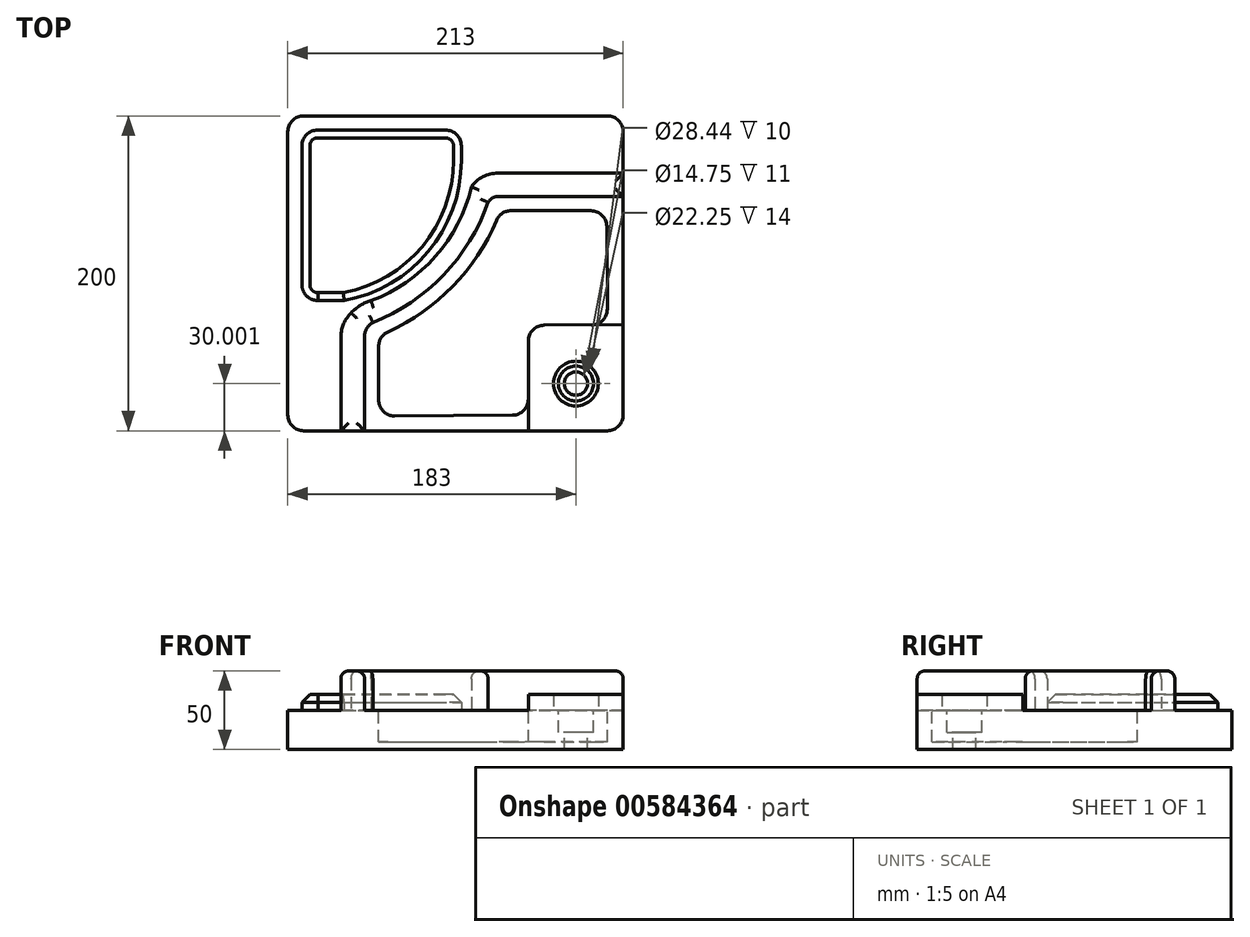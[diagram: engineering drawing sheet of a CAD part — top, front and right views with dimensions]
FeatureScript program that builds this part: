
annotation { "Feature Type Name" : "Feature", "Feature Type Description" : "" }
export const myFeature = defineFeature(function(context is Context, id is Id, definition is map)
    precondition{}
    {
        {
            var Q0;
            Q0=qCreatedBy(makeId("Top.planeOp"),FACE);
            var sketch = newSketch(context, id + "F0", { "sketchPlane" : qUnion([Q0])});
            skLineSegment(sketch, "E0.bottom", {"start": v(10, -74.9) * mm, "end": v(203, -74.9) * mm});
            skLineSegment(sketch, "E0.top", {"start": v(10, 125.1) * mm, "end": v(203, 125.1) * mm});
            skLineSegment(sketch, "E0.left", {"start": v(0, -64.9) * mm, "end": v(0, 115.1) * mm});
            skLineSegment(sketch, "E0.right", {"start": v(213, -64.9) * mm, "end": v(213, 115.1) * mm});
            skPoint(sketch, "E1.visualSharp", {"position": v(0, 125.1) * mm});
            skArc(sketch, "E1.filletArc", {"start": v(10, 125.1) * mm, "mid": v(2.93, 122.16) * mm, "end": v(0, 115.1) * mm});
            skPoint(sketch, "E2.visualSharp", {"position": v(213, 125.1) * mm});
            skArc(sketch, "E2.filletArc", {"start": v(213, 115.1) * mm, "mid": v(210.07, 122.16) * mm, "end": v(203, 125.1) * mm});
            skPoint(sketch, "E3.visualSharp", {"position": v(213, -74.9) * mm});
            skArc(sketch, "E3.filletArc", {"start": v(203, -74.9) * mm, "mid": v(210.07, -71.98) * mm, "end": v(213, -64.9) * mm});
            skPoint(sketch, "E4.visualSharp", {"position": v(0, -74.9) * mm});
            skArc(sketch, "E4.filletArc", {"start": v(0, -64.9) * mm, "mid": v(2.93, -71.98) * mm, "end": v(10, -74.9) * mm});
            skPoint(sketch, "E5.visualSharp", {"position": v(9, 116.1) * mm});
            skLineSegment(sketch, "E6", {"start": v(9, 17.87) * mm, "end": v(9, 106.1) * mm});
            skArc(sketch, "E7.filletArc", {"start": v(19, 116.1) * mm, "mid": v(11.93, 113.16) * mm, "end": v(9, 106.1) * mm});
            skPoint(sketch, "E8.visualSharp", {"position": v(9, 8.33) * mm});
            skArc(sketch, "E8.filletArc", {"start": v(9, 17.87) * mm, "mid": v(12, 10.73) * mm, "end": v(19.18, 7.87) * mm});
            skLineSegment(sketch, "E9", {"start": v(19, 116.1) * mm, "end": v(100.22, 116.1) * mm});
            skLineSegment(sketch, "E10", {"start": v(110.22, 106.1) * mm, "end": v(110.22, 96.79) * mm});
            skArc(sketch, "E11", {"start": v(35.76, 7.87) * mm, "mid": v(89.15, 38.8) * mm, "end": v(110.22, 96.79) * mm});
            skLineSegment(sketch, "E12", {"start": v(35.76, 7.87) * mm, "end": v(19.18, 7.87) * mm});
            skPoint(sketch, "E13.visualSharp", {"position": v(110.22, 116.1) * mm});
            skArc(sketch, "E13.filletArc", {"start": v(110.22, 106.1) * mm, "mid": v(107.3, 113.16) * mm, "end": v(100.22, 116.1) * mm});
            skSolve(sketch);
        }
        {
            var Q0;
            Q0=makeQuery(id+"F0.imprint","IMPRINT",FACE,{"disambiguationData":[TD([[makeQuery(id+"F0.imprint","IMPRINT",EDGE,{"derivedFrom":sQuery(id+"F0.wireOp",EDGE,"E0.bottom")}),1.0]])]});
            extrude(context, id + "F1", {"entities" : qUnion([Q0]), "depth" : 25 * mm, "offsetDistance" : 25 * mm});
        }
        {
            var Q0;
            Q0=makeQuery(id+"F0.imprint","IMPRINT",FACE,{"disambiguationData":[TD([[makeQuery(id+"F0.imprint","IMPRINT",EDGE,{"derivedFrom":sQuery(id+"F0.wireOp",EDGE,"E6")}),-1.0]])]});
            extrude(context, id + "F2", {"entities" : qUnion([Q0]), "operationType" : NewBodyOperationType.ADD, "depth" : 30 * mm, "offsetDistance" : 25 * mm});
        }
        {
            var Q0;
            Q0=makeQuery(id+"F2.opExtrude","CAP_FACE",FACE,{"disambiguationData":[OSD([sQuery(id+"F0.wireOp",EDGE,"3HCnRjnO-4Gxs-uSjP-bO4h-lCZGxT7cbKnb"),sQuery(id+"F0.wireOp",EDGE,"J8DouMNQ-wWCs-JTDe-ndfE-pehenXBLLNa2"),sQuery(id+"F0.wireOp",EDGE,"E6"),sQuery(id+"F0.wireOp",EDGE,"E7.filletArc"),sQuery(id+"F0.wireOp",EDGE,"zigALkeZ-qIqq-vtYU-ptZh-4IW8mXbsAmNO")])],"isStart":false});
            extrude(context, id + "F3", {"entities" : qUnion([Q0]), "operationType" : NewBodyOperationType.ADD, "depth" : 5 * mm, "offsetDistance" : 25 * mm});
        }
        {
            var Q0;
            Q0=makeQuery(id+"F3.opExtrude","CAP_FACE",FACE,{"disambiguationData":[OSD([sQuery(id+"F0.wireOp",EDGE,"3HCnRjnO-4Gxs-uSjP-bO4h-lCZGxT7cbKnb"),sQuery(id+"F0.wireOp",EDGE,"J8DouMNQ-wWCs-JTDe-ndfE-pehenXBLLNa2"),sQuery(id+"F0.wireOp",EDGE,"E6"),sQuery(id+"F0.wireOp",EDGE,"E7.filletArc"),sQuery(id+"F0.wireOp",EDGE,"zigALkeZ-qIqq-vtYU-ptZh-4IW8mXbsAmNO")])],"isStart":false});
            chamfer(context, id + "F4", {"entities" : qUnion([Q0]), "width" : 5 * mm, "tangentPropagation" : true});
        }
        {
            var Q0;
            Q0=makeQuery(id+"F1.opExtrude","CAP_FACE",FACE,{"disambiguationData":[OSD([sQuery(id+"F0.wireOp",EDGE,"E0.bottom"),sQuery(id+"F0.wireOp",EDGE,"E0.top"),sQuery(id+"F0.wireOp",EDGE,"E0.left"),sQuery(id+"F0.wireOp",EDGE,"E0.right"),sQuery(id+"F0.wireOp",EDGE,"E1.filletArc"),sQuery(id+"F0.wireOp",EDGE,"E2.filletArc"),sQuery(id+"F0.wireOp",EDGE,"E3.filletArc"),sQuery(id+"F0.wireOp",EDGE,"E4.filletArc"),sQuery(id+"F0.wireOp",EDGE,"3HCnRjnO-4Gxs-uSjP-bO4h-lCZGxT7cbKnb"),sQuery(id+"F0.wireOp",EDGE,"J8DouMNQ-wWCs-JTDe-ndfE-pehenXBLLNa2"),sQuery(id+"F0.wireOp",EDGE,"E6"),sQuery(id+"F0.wireOp",EDGE,"E7.filletArc"),sQuery(id+"F0.wireOp",EDGE,"zigALkeZ-qIqq-vtYU-ptZh-4IW8mXbsAmNO"),sQuery(id+"F0.wireOp",EDGE,"895f77bc-af32-4142-a491-5c8aeb228727.filletArc"),sQuery(id+"F0.wireOp",EDGE,"E8.filletArc")])],"isStart":false});
            var sketch = newSketch(context, id + "F5", { "sketchPlane" : qUnion([Q0])});
            skLineSegment(sketch, "E14", {"start": v(33.76, -74.9) * mm, "end": v(33.76, -14.9) * mm});
            skLineSegment(sketch, "E15", {"start": v(48.76, -74.9) * mm, "end": v(48.76, -14.9) * mm});
            skLineSegment(sketch, "E16", {"start": v(213, 73.86) * mm, "end": v(153.06, 73.86) * mm});
            skLineSegment(sketch, "E17", {"start": v(154.22, 88.73) * mm, "end": v(213, 88.73) * mm});
            skArc(sketch, "E18", {"start": v(54, -6.13) * mm, "mid": v(50.17, -9.8) * mm, "end": v(48.76, -14.9) * mm});
            skArc(sketch, "E19", {"start": v(52.85, 7.75) * mm, "mid": v(46.05, 4.74) * mm, "end": v(40.31, 0) * mm});
            skArc(sketch, "E20", {"start": v(40.31, 0) * mm, "mid": v(35.47, -6.77) * mm, "end": v(33.76, -14.9) * mm});
            skLineSegment(sketch, "E21", {"start": v(154.22, 88.73) * mm, "end": v(133.4, 88.73) * mm});
            skLineSegment(sketch, "E22", {"start": v(153.06, 73.86) * mm, "end": v(133.4, 73.86) * mm});
            skArc(sketch, "E23", {"start": v(133.4, 88.73) * mm, "mid": v(124.01, 86.45) * mm, "end": v(116.73, 80.12) * mm});
            skArc(sketch, "E24", {"start": v(133.4, 73.86) * mm, "mid": v(129.78, 72.88) * mm, "end": v(127.14, 70.23) * mm});
            skArc(sketch, "E25", {"start": v(52.85, 7.75) * mm, "mid": v(93.86, 35.93) * mm, "end": v(116.73, 80.12) * mm});
            skArc(sketch, "E26", {"start": v(54, -6.13) * mm, "mid": v(98.93, 24.05) * mm, "end": v(127.14, 70.23) * mm});
            skLineSegment(sketch, "E27", {"start": v(192.6, 64.86) * mm, "end": v(141.76, 64.86) * mm});
            skArc(sketch, "E28", {"start": v(63.63, -12.03) * mm, "mid": v(104.76, 16.86) * mm, "end": v(132.54, 58.74) * mm});
            skLineSegment(sketch, "E29", {"start": v(57.76, -21.14) * mm, "end": v(57.76, -55.46) * mm});
            skLineSegment(sketch, "E30", {"start": v(67.83, -65.46) * mm, "end": v(142.83, -64.97) * mm});
            skLineSegment(sketch, "E31", {"start": v(152.76, -54.97) * mm, "end": v(152.76, -17.88) * mm});
            skLineSegment(sketch, "E32", {"start": v(162.7, -7.88) * mm, "end": v(193, -7.69) * mm});
            skLineSegment(sketch, "E33", {"start": v(202.93, 2.38) * mm, "end": v(202.6, 54.92) * mm});
            skPoint(sketch, "E34.visualSharp", {"position": v(57.76, -14.53) * mm});
            skArc(sketch, "E34.filletArc", {"start": v(63.63, -12.03) * mm, "mid": v(59.36, -15.72) * mm, "end": v(57.76, -21.14) * mm});
            skPoint(sketch, "E35.visualSharp", {"position": v(134.95, 64.86) * mm});
            skArc(sketch, "E35.filletArc", {"start": v(141.76, 64.86) * mm, "mid": v(136.23, 63.19) * mm, "end": v(132.54, 58.74) * mm});
            skPoint(sketch, "E36.visualSharp", {"position": v(202.53, 64.86) * mm});
            skArc(sketch, "E36.filletArc", {"start": v(202.6, 54.92) * mm, "mid": v(199.64, 61.95) * mm, "end": v(192.6, 64.86) * mm});
            skPoint(sketch, "E37.visualSharp", {"position": v(203, -7.62) * mm});
            skArc(sketch, "E37.filletArc", {"start": v(193, -7.69) * mm, "mid": v(200.05, -4.71) * mm, "end": v(202.93, 2.38) * mm});
            skPoint(sketch, "E38.visualSharp", {"position": v(152.76, -7.95) * mm});
            skArc(sketch, "E38.filletArc", {"start": v(162.7, -7.88) * mm, "mid": v(155.67, -10.84) * mm, "end": v(152.76, -17.88) * mm});
            skPoint(sketch, "E39.visualSharp", {"position": v(152.76, -64.9) * mm});
            skArc(sketch, "E39.filletArc", {"start": v(142.83, -64.97) * mm, "mid": v(149.85, -62.02) * mm, "end": v(152.76, -54.97) * mm});
            skPoint(sketch, "E40.visualSharp", {"position": v(57.76, -65.53) * mm});
            skArc(sketch, "E40.filletArc", {"start": v(57.76, -55.46) * mm, "mid": v(60.71, -62.56) * mm, "end": v(67.83, -65.46) * mm});
            skLineSegment(sketch, "E41", {"start": v(152.76, -54.97) * mm, "end": v(152.76, -74.9) * mm});
            skLineSegment(sketch, "E42", {"start": v(193, -7.69) * mm, "end": v(213, -7.56) * mm});
            skPoint(sketch, "E43", {"position": v(183, -44.9) * mm});
            skLineSegment(sketch, "E44", {"start": v(183, -44.9) * mm, "end": v(183, -74.9) * mm, "construction": true});
            skLineSegment(sketch, "E45", {"start": v(183, -44.9) * mm, "end": v(213, -44.9) * mm, "construction": true});
            skCircle(sketch, "E46", {"center": v(183, -44.9) * mm, "radius": 14.22 * mm});
            skSolve(sketch);
        }
        {
            var Q0;
            {var subQ0=sQuery(id+"F5.wireOp",EDGE,"E14");Q0=makeQuery(id+"F5.imprint","IMPRINT",FACE,{"disambiguationData":[TD([[makeQuery(id+"F5.imprint","IMPRINT",EDGE,{"derivedFrom":subQ0}),-1.0]])]});}
            extrude(context, id + "F6", {"entities" : qUnion([Q0]), "operationType" : NewBodyOperationType.ADD, "depth" : 25 * mm, "offsetDistance" : 25 * mm});
        }
        {
            var Q0;
            Q0=makeQuery(id+"F5.imprint","IMPRINT",FACE,{"disambiguationData":[TD([[makeQuery(id+"F5.imprint","IMPRINT",EDGE,{"derivedFrom":sQuery(id+"F5.wireOp",EDGE,"E27")}),1.0]])]});
            extrude(context, id + "F7", {"entities" : qUnion([Q0]), "operationType" : NewBodyOperationType.REMOVE, "oppositeDirection" : true, "depth" : 20 * mm, "offsetDistance" : 25 * mm});
        }
        {
            var Q0;
            Q0=makeQuery(id+"F5.imprint","IMPRINT",FACE,{"disambiguationData":[TD([[makeQuery(id+"F5.imprint","IMPRINT",EDGE,{"derivedFrom":sQuery(id+"F5.wireOp",EDGE,"E31")}),-1.0]])]});
            extrude(context, id + "F8", {"entities" : qUnion([Q0]), "operationType" : NewBodyOperationType.ADD, "depth" : 10 * mm, "offsetDistance" : 25 * mm});
        }
        {
            var Q0;
            Q0=sQuery(id+"F5.wireOp",VERTEX,"E43");
            var Q1;
            Q1=makeQuery(id+"F1.opExtrude","SWEPT_BODY",BODY,{"disambiguationData":[OSD([sQuery(id+"F0.wireOp",EDGE,"E0.bottom"),sQuery(id+"F0.wireOp",EDGE,"E0.top"),sQuery(id+"F0.wireOp",EDGE,"E0.left"),sQuery(id+"F0.wireOp",EDGE,"E0.right"),sQuery(id+"F0.wireOp",EDGE,"E1.filletArc"),sQuery(id+"F0.wireOp",EDGE,"E2.filletArc"),sQuery(id+"F0.wireOp",EDGE,"E3.filletArc"),sQuery(id+"F0.wireOp",EDGE,"E4.filletArc"),sQuery(id+"F0.wireOp",EDGE,"E6"),sQuery(id+"F0.wireOp",EDGE,"E7.filletArc"),sQuery(id+"F0.wireOp",EDGE,"E8.filletArc"),sQuery(id+"F0.wireOp",EDGE,"E9"),sQuery(id+"F0.wireOp",EDGE,"E10"),sQuery(id+"F0.wireOp",EDGE,"E11"),sQuery(id+"F0.wireOp",EDGE,"E12"),sQuery(id+"F0.wireOp",EDGE,"E13.filletArc")])]});
            hole(context, id + "F9", {"style" : HoleStyle.C_BORE, "endStyle" : HoleEndStyle.THROUGH, "standardTappedOrClearance" : lookupTablePath({ "standard" : "ISO", "fit" : "Close", "size" : "M14", "type" : "Clearance" }), "standardBlindInLast" : lookupTablePath({ "fit" : "Close", "standard" : "ISO", "size" : "M14", "type" : "Clearance" }), "holeDiameter" : 14.75 * mm, "cBoreDiameter" : 22.25 * mm, "cBoreDepth" : 14 * mm, "majorDiameter" : 5 * mm, "isTappedThrough" : true, "tappedDepth" : 12 * mm, "tapClearance" : 3, "locations" : qUnion([Q0]), "scope" : qUnion([Q1])});
        }
        {
            var Q0;
            Q0=makeQuery(id+"F6.opExtrude","CAP_FACE",FACE,{"disambiguationData":[OSD([sQuery(id+"F0.wireOp",EDGE,"E0.bottom"),sQuery(id+"F0.wireOp",EDGE,"E0.right"),sQuery(id+"F5.wireOp",EDGE,"E14"),sQuery(id+"F5.wireOp",EDGE,"E15"),sQuery(id+"F5.wireOp",EDGE,"E16"),sQuery(id+"F5.wireOp",EDGE,"E17"),sQuery(id+"F5.wireOp",EDGE,"E18"),sQuery(id+"F5.wireOp",EDGE,"E19"),sQuery(id+"F5.wireOp",EDGE,"E20"),sQuery(id+"F5.wireOp",EDGE,"E21"),sQuery(id+"F5.wireOp",EDGE,"E22"),sQuery(id+"F5.wireOp",EDGE,"E23"),sQuery(id+"F5.wireOp",EDGE,"E24"),sQuery(id+"F5.wireOp",EDGE,"E25"),sQuery(id+"F5.wireOp",EDGE,"E26")])],"isStart":false});
            fillet(context, id + "F10", {"entities" : qUnion([Q0]), "radius" : 5 * mm, "tangentPropagation" : true, "allowEdgeOverflow" : false});
        }
    });
